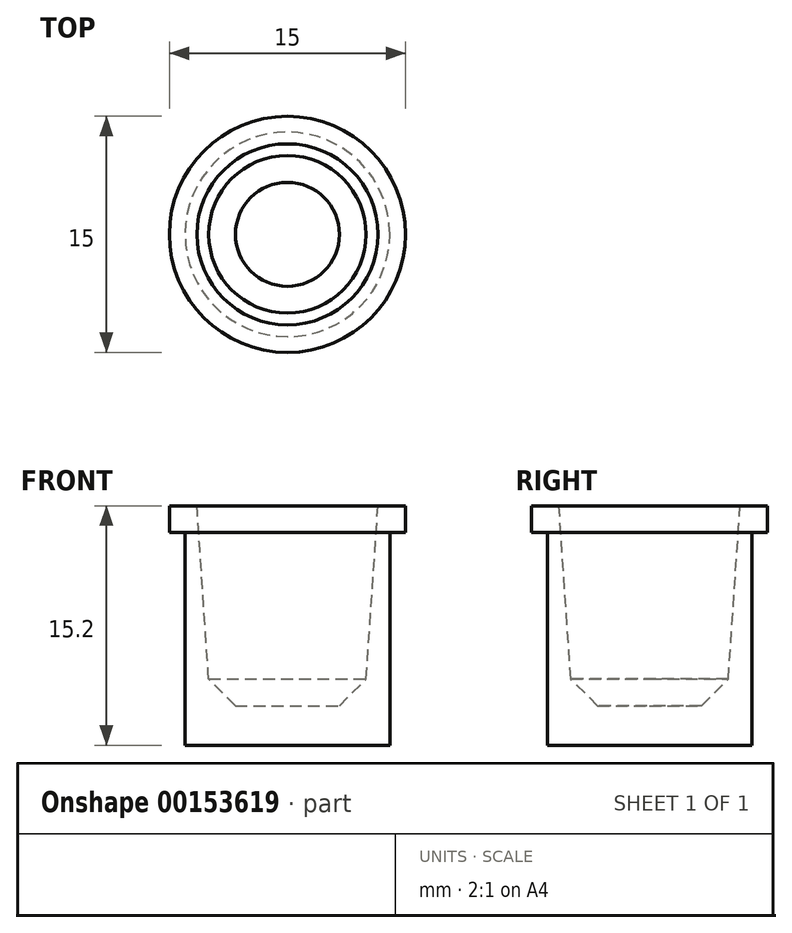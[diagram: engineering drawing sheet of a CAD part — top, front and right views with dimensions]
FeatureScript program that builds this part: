
annotation { "Feature Type Name" : "Feature", "Feature Type Description" : "" }
export const myFeature = defineFeature(function(context is Context, id is Id, definition is map)
    precondition{}
    {
        {
            var Q0;
            Q0=qCreatedBy(makeId("Front.planeOp"),FACE);
            var sketch = newSketch(context, id + "F0", { "sketchPlane" : qUnion([Q0])});
            skLineSegment(sketch, "E0", {"start": v(0, 0) * mm, "end": v(-3.3, 0) * mm});
            skLineSegment(sketch, "E1", {"start": v(-3.3, 0) * mm, "end": v(-5, 1.7) * mm});
            skLineSegment(sketch, "E2", {"start": v(-5, 1.7) * mm, "end": v(-5.75, 12.7) * mm});
            skLineSegment(sketch, "E3", {"start": v(-5.75, 12.7) * mm, "end": v(-7.5, 12.7) * mm});
            skLineSegment(sketch, "E4", {"start": v(-7.5, 12.7) * mm, "end": v(-7.5, 11) * mm});
            skLineSegment(sketch, "E5", {"start": v(-7.5, 11) * mm, "end": v(-6.5, 11) * mm});
            skLineSegment(sketch, "E6", {"start": v(-6.5, 11) * mm, "end": v(-6.5, -2.5) * mm});
            skLineSegment(sketch, "E7", {"start": v(-6.5, -2.5) * mm, "end": v(0, -2.5) * mm});
            skLineSegment(sketch, "E8", {"start": v(0, -2.5) * mm, "end": v(0, 0) * mm});
            skSolve(sketch);
        }
        {
            var Q0;
            Q0=makeQuery(id+"F0.imprint","IMPRINT",FACE,{"disambiguationData":[TD([[makeQuery(id+"F0.imprint","IMPRINT",EDGE,{"derivedFrom":sQuery(id+"F0.wireOp",EDGE,"E0")}),1.0]])]});
            var Q1;
            Q1=sQuery(id+"F0.wireOp",EDGE,"E8");
            revolve(context, id + "F1", {"entities" : qUnion([Q0]), "axis" : qUnion([Q1]), "revolveType" : RevolveType.FULL});
        }
    });
